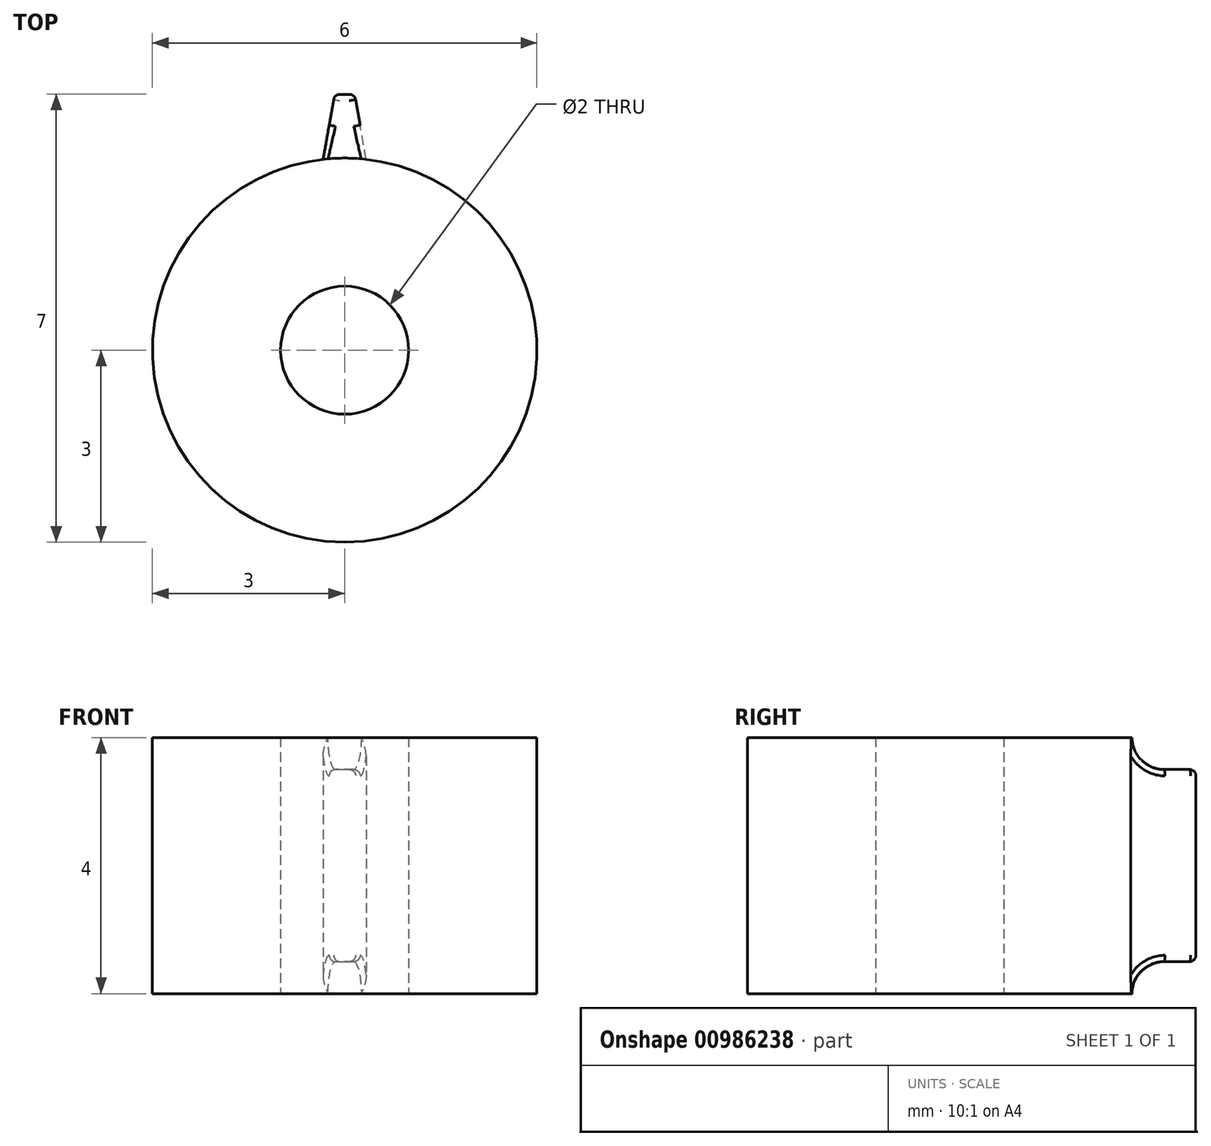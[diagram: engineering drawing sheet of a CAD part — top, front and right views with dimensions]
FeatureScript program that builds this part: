
annotation { "Feature Type Name" : "Feature", "Feature Type Description" : "" }
export const myFeature = defineFeature(function(context is Context, id is Id, definition is map)
    precondition{}
    {
        {
            var Q0;
            Q0=qCreatedBy(makeId("Top.planeOp"),FACE);
            var sketch = newSketch(context, id + "F0", { "sketchPlane" : qUnion([Q0])});
            skCircle(sketch, "E0", {"center": v(0, 0) * mm, "radius": 3 * mm});
            skCircle(sketch, "E1", {"center": v(0, 0) * mm, "radius": 1 * mm});
            skSolve(sketch);
        }
        {
            var Q0;
            Q0=makeQuery(id+"F0.imprint","IMPRINT",FACE,{"disambiguationData":[TD([[makeQuery(id+"F0.imprint","IMPRINT",EDGE,{"derivedFrom":sQuery(id+"F0.wireOp",EDGE,"E0")}),1.0]])]});
            extrude(context, id + "F1", {"entities" : qUnion([Q0]), "endBound" : BoundingType.SYMMETRIC, "depth" : 4 * mm, "offsetDistance" : 25 * mm});
        }
        {
            var Q0;
            Q0=qCreatedBy(makeId("Top.planeOp"),FACE);
            var sketch = newSketch(context, id + "F2", { "sketchPlane" : qUnion([Q0])});
            skLineSegment(sketch, "E2", {"start": v(0, 0) * mm, "end": v(0, 4) * mm, "construction": true});
            skCircle(sketch, "E3", {"center": v(0, 0) * mm, "radius": 4 * mm, "construction": true});
            skLineSegment(sketch, "E4", {"start": v(-0.34, 2.98) * mm, "end": v(-0.16, 4) * mm});
            skLineSegment(sketch, "E5", {"start": v(-0.16, 4) * mm, "end": v(0.16, 4) * mm});
            skLineSegment(sketch, "E6", {"start": v(0.16, 4) * mm, "end": v(0.34, 2.98) * mm});
            skLineSegment(sketch, "E7", {"start": v(0.34, 2.98) * mm, "end": v(-0.34, 2.98) * mm});
            skLineSegment(sketch, "E8", {"start": v(0, 0) * mm, "end": v(-0.34, 2.98) * mm, "construction": true});
            skLineSegment(sketch, "E9", {"start": v(0, 0) * mm, "end": v(0.34, 2.98) * mm, "construction": true});
            skSolve(sketch);
        }
        {
            var Q0;
            Q0 = qSketchRegion(id + "F2", true);
            extrude(context, id + "F3", {"entities" : qUnion([Q0]), "operationType" : NewBodyOperationType.ADD, "endBound" : BoundingType.SYMMETRIC, "depth" : 3 * mm, "offsetDistance" : 25 * mm});
        }
        {
            var Q0;
            Q0=makeQuery(id+"F3.opExtrude","SWEPT_EDGE",EDGE,{"disambiguationData":[OSD([sQuery(id+"F2.wireOp",EDGE,"E4"),sQuery(id+"F2.wireOp",EDGE,"E5")])]});
            var Q1;
            Q1=makeQuery(id+"F3.opExtrude","SWEPT_EDGE",EDGE,{"disambiguationData":[OSD([sQuery(id+"F2.wireOp",EDGE,"E5"),sQuery(id+"F2.wireOp",EDGE,"E6")])]});
            fillet(context, id + "F4", {"entities" : qUnion([Q0, Q1]), "radius" : 0.1 * mm, "tangentPropagation" : true, "allowEdgeOverflow" : false});
        }
        {
            var Q0;
            Q0=makeQuery(id+"F3.opExtrude","SWEPT_EDGE",EDGE,{"disambiguationData":[OSD([sQuery(id+"F2.wireOp",EDGE,"E4"),sQuery(id+"F2.wireOp",EDGE,"E7")])]});
            var Q1;
            Q1=makeQuery(id+"F3.boolean.opBoolean","INTERSECT",EDGE,{"derivedFrom":[makeQuery(id+"F1.opExtrude","SWEPT_FACE",FACE,{"disambiguationData":[OSD([sQuery(id+"F0.wireOp",EDGE,"E0")])]}),makeQuery(id+"F3.opExtrude","CAP_FACE",FACE,{"disambiguationData":[OSD([sQuery(id+"F2.wireOp",EDGE,"E4"),sQuery(id+"F2.wireOp",EDGE,"E5"),sQuery(id+"F2.wireOp",EDGE,"E6"),sQuery(id+"F2.wireOp",EDGE,"E7")])],"isStart":false})]});
            var Q2;
            Q2=makeQuery(id+"F3.opExtrude","SWEPT_EDGE",EDGE,{"disambiguationData":[OSD([sQuery(id+"F2.wireOp",EDGE,"E6"),sQuery(id+"F2.wireOp",EDGE,"E7")])]});
            var Q3;
            Q3=makeQuery(id+"F3.boolean.opBoolean","INTERSECT",EDGE,{"derivedFrom":[makeQuery(id+"F1.opExtrude","SWEPT_FACE",FACE,{"disambiguationData":[OSD([sQuery(id+"F0.wireOp",EDGE,"E0")])]}),makeQuery(id+"F3.opExtrude","CAP_FACE",FACE,{"disambiguationData":[OSD([sQuery(id+"F2.wireOp",EDGE,"E4"),sQuery(id+"F2.wireOp",EDGE,"E5"),sQuery(id+"F2.wireOp",EDGE,"E6"),sQuery(id+"F2.wireOp",EDGE,"E7")])],"isStart":true})]});
            fillet(context, id + "F5", {"entities" : qUnion([Q0, Q1, Q2, Q3]), "radius" : 0.5 * mm, "tangentPropagation" : true, "allowEdgeOverflow" : false});
        }
        {
            var Q0;
            Q0=makeQuery(id+"F3.opExtrude","CAP_EDGE",EDGE,{"disambiguationData":[OSD([sQuery(id+"F2.wireOp",EDGE,"E4")])],"isStart":false});
            var Q1;
            Q1=makeQuery(id+"F3.opExtrude","CAP_EDGE",EDGE,{"disambiguationData":[OSD([sQuery(id+"F2.wireOp",EDGE,"E4")])],"isStart":true});
            var Q2;
            Q2=makeQuery(id+"F3.opExtrude","CAP_EDGE",EDGE,{"disambiguationData":[OSD([sQuery(id+"F2.wireOp",EDGE,"E6")])],"isStart":false});
            var Q3;
            Q3=makeQuery(id+"F3.opExtrude","CAP_EDGE",EDGE,{"disambiguationData":[OSD([sQuery(id+"F2.wireOp",EDGE,"E5")])],"isStart":true});
            fillet(context, id + "F6", {"entities" : qUnion([Q0, Q1, Q2, Q3]), "radius" : 0.1 * mm, "tangentPropagation" : true, "allowEdgeOverflow" : false});
        }
    });
